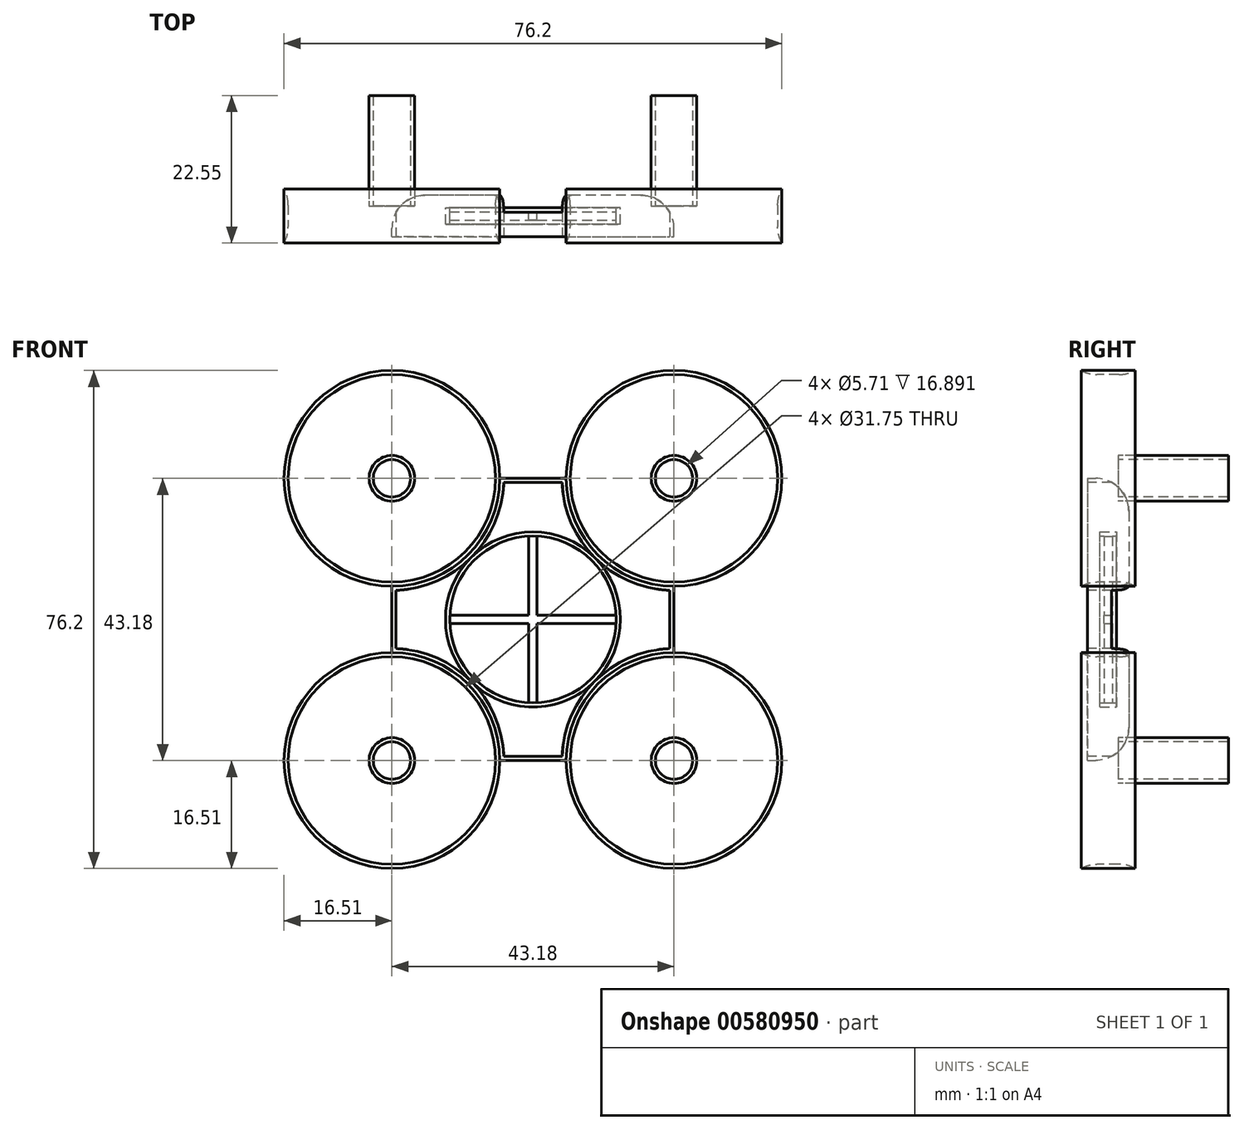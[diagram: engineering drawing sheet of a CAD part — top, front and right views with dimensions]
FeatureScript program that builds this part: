
annotation { "Feature Type Name" : "Feature", "Feature Type Description" : "" }
export const myFeature = defineFeature(function(context is Context, id is Id, definition is map)
    precondition{}
    {
        {
            var Q0;
            Q0=qCreatedBy(makeId("Front.planeOp"),FACE);
            var sketch = newSketch(context, id + "F0", { "sketchPlane" : qUnion([Q0])});
            skPoint(sketch, "E0.middle", {"position": v(0, 0) * mm});
            skCircle(sketch, "E1", {"center": v(-21.6, 21.59) * mm, "radius": 16.51 * mm});
            skCircle(sketch, "E2.1.0", {"center": v(21.59, 21.6) * mm, "radius": 16.51 * mm});
            skCircle(sketch, "E2.2.0", {"center": v(21.6, -21.59) * mm, "radius": 16.51 * mm});
            skCircle(sketch, "E2.3.0", {"center": v(-21.59, -21.6) * mm, "radius": 16.51 * mm});
            skLineSegment(sketch, "E3.bottom", {"start": v(5.08, 21.6) * mm, "end": v(-5.08, 21.6) * mm});
            skLineSegment(sketch, "E3.top", {"start": v(5.08, -21.6) * mm, "end": v(-5.08, -21.6) * mm});
            skLineSegment(sketch, "E3.left", {"start": v(21.59, 5.08) * mm, "end": v(21.59, -5.08) * mm});
            skLineSegment(sketch, "E3.right", {"start": v(-21.59, 5.08) * mm, "end": v(-21.59, -5.08) * mm});
            skPoint(sketch, "E4.orphan", {"position": v(-21.59, 21.6) * mm});
            skPoint(sketch, "E5.orphan", {"position": v(21.59, -21.6) * mm});
            skSolve(sketch);
        }
        {
            var Q0;
            {var subQ0=sQuery(id+"F0.wireOp",EDGE,"E1");var subQ1=makeQuery(id+"F0.imprint","INTERSECT",VERTEX,{"derivedFrom":[subQ0,sQuery(id+"F0.wireOp",EDGE,"E3.bottom")]});Q0=makeQuery(id+"F0.imprint","IMPRINT",FACE,{"disambiguationData":[TD([[makeQuery(id+"F0.imprint","IMPRINT",EDGE,{"disambiguationData":[TD([[subQ1,-1.0]])],"derivedFrom":subQ0}),1.0]])]});}
            var Q1;
            {var subQ0=sQuery(id+"F0.wireOp",EDGE,"E2.3.0");var subQ1=makeQuery(id+"F0.imprint","INTERSECT",VERTEX,{"derivedFrom":[subQ0,sQuery(id+"F0.wireOp",EDGE,"E3.top")]});Q1=makeQuery(id+"F0.imprint","IMPRINT",FACE,{"disambiguationData":[TD([[makeQuery(id+"F0.imprint","IMPRINT",EDGE,{"disambiguationData":[TD([[subQ1,1.0]])],"derivedFrom":subQ0}),1.0]])]});}
            var Q2;
            {var subQ0=sQuery(id+"F0.wireOp",EDGE,"E2.2.0");var subQ1=makeQuery(id+"F0.imprint","INTERSECT",VERTEX,{"derivedFrom":[subQ0,sQuery(id+"F0.wireOp",EDGE,"E3.top")]});Q2=makeQuery(id+"F0.imprint","IMPRINT",FACE,{"disambiguationData":[TD([[makeQuery(id+"F0.imprint","IMPRINT",EDGE,{"disambiguationData":[TD([[subQ1,-1.0]])],"derivedFrom":subQ0}),1.0]])]});}
            var Q3;
            {var subQ0=sQuery(id+"F0.wireOp",EDGE,"E2.1.0");var subQ1=makeQuery(id+"F0.imprint","INTERSECT",VERTEX,{"derivedFrom":[subQ0,sQuery(id+"F0.wireOp",EDGE,"E3.bottom")]});Q3=makeQuery(id+"F0.imprint","IMPRINT",FACE,{"disambiguationData":[TD([[makeQuery(id+"F0.imprint","IMPRINT",EDGE,{"disambiguationData":[TD([[subQ1,1.0]])],"derivedFrom":subQ0}),1.0]])]});}
            extrude(context, id + "F1", {"entities" : qUnion([Q0, Q1, Q2, Q3]), "depth" : 8.25 * mm, "offsetDistance" : 25.4 * mm, "symmetric" : true});
        }
        {
            var Q0;
            {var subQ5=sQuery(id+"F0.wireOp",EDGE,"E3.bottom");Q0=makeQuery(id+"F0.imprint","IMPRINT",FACE,{"disambiguationData":[TD([[makeQuery(id+"F0.imprint","IMPRINT",EDGE,{"derivedFrom":subQ5}),1.0]])]});}
            extrude(context, id + "F2", {"entities" : qUnion([Q0]), "depth" : 6.35 * mm, "offsetDistance" : 25.4 * mm, "symmetric" : true});
        }
        {
            var Q0;
            Q0=makeQuery(id+"F1.opExtrude","CAP_FACE",FACE,{"disambiguationData":[OSD([sQuery(id+"F0.wireOp",EDGE,"E1")])],"isStart":false});
            var sketch = newSketch(context, id + "F3", { "sketchPlane" : qUnion([Q0])});
            skCircle(sketch, "E6", {"center": v(-21.6, 21.59) * mm, "radius": 15.88 * mm});
            skCircle(sketch, "E7.1.0", {"center": v(21.59, 21.6) * mm, "radius": 15.88 * mm});
            skCircle(sketch, "E7.2.0", {"center": v(21.6, -21.59) * mm, "radius": 15.88 * mm});
            skCircle(sketch, "E7.3.0", {"center": v(-21.59, -21.6) * mm, "radius": 15.88 * mm});
            skPoint(sketch, "E7.center", {"position": v(0, 0) * mm});
            skLineSegment(sketch, "E7.anchor1", {"start": v(0, 0) * mm, "end": v(-21.6, 21.59) * mm, "construction": true});
            skLineSegment(sketch, "E7.anchor2", {"start": v(0, 0) * mm, "end": v(-21.59, -21.6) * mm, "construction": true});
            skSolve(sketch);
        }
        {
            var Q0;
            Q0=makeQuery(id+"F3.imprint","IMPRINT",FACE,{"disambiguationData":[TD([[makeQuery(id+"F3.imprint","IMPRINT",EDGE,{"derivedFrom":sQuery(id+"F3.wireOp",EDGE,"E6")}),1.0]])]});
            var Q1;
            Q1=makeQuery(id+"F3.imprint","IMPRINT",FACE,{"disambiguationData":[TD([[makeQuery(id+"F3.imprint","IMPRINT",EDGE,{"derivedFrom":sQuery(id+"F3.wireOp",EDGE,"E7.1.0")}),1.0]])]});
            var Q2;
            Q2=makeQuery(id+"F3.imprint","IMPRINT",FACE,{"disambiguationData":[TD([[makeQuery(id+"F3.imprint","IMPRINT",EDGE,{"derivedFrom":sQuery(id+"F3.wireOp",EDGE,"E7.2.0")}),1.0]])]});
            var Q3;
            Q3=makeQuery(id+"F3.imprint","IMPRINT",FACE,{"disambiguationData":[TD([[makeQuery(id+"F3.imprint","IMPRINT",EDGE,{"derivedFrom":sQuery(id+"F3.wireOp",EDGE,"E7.3.0")}),1.0]])]});
            extrude(context, id + "F4", {"entities" : qUnion([Q0, Q1, Q2, Q3]), "operationType" : NewBodyOperationType.REMOVE, "oppositeDirection" : true, "depth" : 25.4 * mm, "offsetDistance" : 25.4 * mm});
        }
        {
            var Q0;
            Q0=makeQuery(id+"F2.opExtrude","CAP_FACE",FACE,{"disambiguationData":[OSD([sQuery(id+"F0.wireOp",EDGE,"E1"),sQuery(id+"F0.wireOp",EDGE,"E2.1.0"),sQuery(id+"F0.wireOp",EDGE,"E2.2.0"),sQuery(id+"F0.wireOp",EDGE,"E2.3.0"),sQuery(id+"F0.wireOp",EDGE,"E3.bottom"),sQuery(id+"F0.wireOp",EDGE,"E3.top"),sQuery(id+"F0.wireOp",EDGE,"E3.left"),sQuery(id+"F0.wireOp",EDGE,"E3.right")])],"isStart":false});
            var sketch = newSketch(context, id + "F5", { "sketchPlane" : qUnion([Q0])});
            skLineSegment(sketch, "E8.0", {"start": v(4.46, 20.96) * mm, "end": v(-4.46, 20.96) * mm});
            skArc(sketch, "E8.1", {"start": v(20.95, 4.46) * mm, "mid": v(9.47, 9.47) * mm, "end": v(4.46, 20.96) * mm});
            skArc(sketch, "E8.2", {"start": v(-4.46, 20.96) * mm, "mid": v(-9.47, 9.47) * mm, "end": v(-20.95, 4.46) * mm});
            skLineSegment(sketch, "E8.3", {"start": v(20.95, -4.46) * mm, "end": v(20.95, 4.46) * mm});
            skLineSegment(sketch, "E8.4", {"start": v(-20.95, 4.46) * mm, "end": v(-20.95, -4.46) * mm});
            skArc(sketch, "E8.5", {"start": v(-20.95, -4.46) * mm, "mid": v(-9.47, -9.47) * mm, "end": v(-4.46, -20.96) * mm});
            skLineSegment(sketch, "E8.6", {"start": v(-4.46, -20.96) * mm, "end": v(4.46, -20.96) * mm});
            skArc(sketch, "E8.7", {"start": v(4.46, -20.96) * mm, "mid": v(9.47, -9.47) * mm, "end": v(20.95, -4.46) * mm});
            skSolve(sketch);
        }
        {
            var Q0;
            Q0=makeQuery(id+"F5.imprint","IMPRINT",FACE,{"disambiguationData":[TD([[makeQuery(id+"F5.imprint","IMPRINT",EDGE,{"derivedFrom":sQuery(id+"F5.wireOp",EDGE,"E8.0")}),1.0]])]});
            extrude(context, id + "F6", {"entities" : qUnion([Q0]), "operationType" : NewBodyOperationType.REMOVE, "oppositeDirection" : true, "depth" : 25.4 * mm, "offsetDistance" : 25.4 * mm});
        }
        {
            var Q0;
            Q0=makeQuery(id+"F4.boolean.opBoolean","COPY",FACE,{"derivedFrom":makeQuery(id+"F4.opExtrude","SWEPT_FACE",FACE,{"disambiguationData":[OSD([sQuery(id+"F3.wireOp",EDGE,"E7.1.0")])]})});
            var Q1;
            Q1=makeQuery(id+"F4.boolean.opBoolean","COPY",FACE,{"derivedFrom":makeQuery(id+"F4.opExtrude","SWEPT_FACE",FACE,{"disambiguationData":[OSD([sQuery(id+"F3.wireOp",EDGE,"E7.2.0")])]})});
            var Q2;
            Q2=makeQuery(id+"F4.boolean.opBoolean","COPY",FACE,{"derivedFrom":makeQuery(id+"F4.opExtrude","SWEPT_FACE",FACE,{"disambiguationData":[OSD([sQuery(id+"F3.wireOp",EDGE,"E6")])]})});
            var Q3;
            Q3=makeQuery(id+"F4.boolean.opBoolean","COPY",FACE,{"derivedFrom":makeQuery(id+"F4.opExtrude","SWEPT_FACE",FACE,{"disambiguationData":[OSD([sQuery(id+"F3.wireOp",EDGE,"E7.3.0")])]})});
            fillet(context, id + "F7", {"entities" : qUnion([Q0, Q1, Q2, Q3]), "radius" : 5.08 * mm, "tangentPropagation" : true, "allowEdgeOverflow" : false});
        }
        {
            var Q0;
            Q0=makeQuery(id+"F2.opExtrude","CAP_EDGE",EDGE,{"disambiguationData":[OSD([sQuery(id+"F0.wireOp",EDGE,"E3.bottom")])],"isStart":true});
            var Q1;
            Q1=makeQuery(id+"F2.opExtrude","CAP_EDGE",EDGE,{"disambiguationData":[OSD([sQuery(id+"F0.wireOp",EDGE,"E3.left")])],"isStart":true});
            var Q2;
            Q2=makeQuery(id+"F2.opExtrude","CAP_EDGE",EDGE,{"disambiguationData":[OSD([sQuery(id+"F0.wireOp",EDGE,"E3.right")])],"isStart":true});
            var Q3;
            Q3=makeQuery(id+"F2.opExtrude","CAP_EDGE",EDGE,{"disambiguationData":[OSD([sQuery(id+"F0.wireOp",EDGE,"E3.top")])],"isStart":true});
            fillet(context, id + "F8", {"entities" : qUnion([Q0, Q1, Q2, Q3]), "radius" : 5.08 * mm, "tangentPropagation" : true, "allowEdgeOverflow" : false});
        }
        {
            var Q0;
            Q0=qCreatedBy(makeId("Front.planeOp"),FACE);
            var sketch = newSketch(context, id + "F9", { "sketchPlane" : qUnion([Q0])});
            skCircle(sketch, "E9", {"center": v(0, 0) * mm, "radius": 13.39 * mm});
            skCircle(sketch, "E10", {"center": v(0, 0) * mm, "radius": 12.75 * mm});
            skLineSegment(sketch, "E11.0", {"start": v(-12.73, -0.64) * mm, "end": v(-0.64, -0.64) * mm});
            skLineSegment(sketch, "E12.0", {"start": v(-12.73, 0.64) * mm, "end": v(-0.64, 0.64) * mm});
            skLineSegment(sketch, "E13.0", {"start": v(-0.64, 12.73) * mm, "end": v(-0.64, 0.64) * mm});
            skLineSegment(sketch, "E14.0", {"start": v(0.63, 12.73) * mm, "end": v(0.64, 0.64) * mm});
            skLineSegment(sketch, "E15.trimOffspring", {"start": v(0.64, 0.64) * mm, "end": v(12.73, 0.64) * mm});
            skLineSegment(sketch, "E16.trimOffspring", {"start": v(0.64, -0.64) * mm, "end": v(12.73, -0.64) * mm});
            skLineSegment(sketch, "E17.trimOffspring", {"start": v(-0.64, -0.64) * mm, "end": v(-0.63, -12.73) * mm});
            skLineSegment(sketch, "E18.trimOffspring", {"start": v(0.64, -0.64) * mm, "end": v(0.64, -12.73) * mm});
            skLineSegment(sketch, "E19", {"start": v(-20.95, 0) * mm, "end": v(20.95, 0) * mm, "construction": true});
            skLineSegment(sketch, "E20", {"start": v(0, 20.96) * mm, "end": v(0, -20.96) * mm, "construction": true});
            skSolve(sketch);
        }
        {
            var Q0;
            Q0=makeQuery(id+"F9.imprint","IMPRINT",FACE,{"disambiguationData":[TD([[makeQuery(id+"F9.imprint","IMPRINT",EDGE,{"derivedFrom":sQuery(id+"F9.wireOp",EDGE,"E10")}),-1.0]])]});
            extrude(context, id + "F10", {"entities" : qUnion([Q0]), "depth" : 2.54 * mm, "offsetDistance" : 25.4 * mm, "symmetric" : true});
        }
        {
            var Q0;
            {var subQ4=sQuery(id+"F9.wireOp",EDGE,"E11.0");Q0=makeQuery(id+"F9.imprint","IMPRINT",FACE,{"disambiguationData":[TD([[makeQuery(id+"F9.imprint","IMPRINT",EDGE,{"derivedFrom":subQ4}),1.0]])]});}
            extrude(context, id + "F11", {"entities" : qUnion([Q0]), "operationType" : NewBodyOperationType.ADD, "depth" : 1.27 * mm, "offsetDistance" : 25.4 * mm, "symmetric" : true});
        }
        {
            var Q0;
            Q0=makeQuery(id+"F8.opFillet","SPLIT",FACE,{"disambiguationData":[OD(0.0)],"derivedFrom":makeQuery(id+"F2.opExtrude","CAP_FACE",FACE,{"disambiguationData":[OSD([sQuery(id+"F0.wireOp",EDGE,"E1"),sQuery(id+"F0.wireOp",EDGE,"E2.1.0"),sQuery(id+"F0.wireOp",EDGE,"E2.2.0"),sQuery(id+"F0.wireOp",EDGE,"E2.3.0"),sQuery(id+"F0.wireOp",EDGE,"E3.bottom"),sQuery(id+"F0.wireOp",EDGE,"E3.top"),sQuery(id+"F0.wireOp",EDGE,"E3.left"),sQuery(id+"F0.wireOp",EDGE,"E3.right")])],"isStart":true})});
            var sketch = newSketch(context, id + "F12", { "sketchPlane" : qUnion([Q0])});
            skCircle(sketch, "E21", {"center": v(21.6, 21.59) * mm, "radius": 2.86 * mm});
            skCircle(sketch, "E22.1.0", {"center": v(-21.59, 21.6) * mm, "radius": 2.86 * mm});
            skCircle(sketch, "E22.2.0", {"center": v(-21.6, -21.59) * mm, "radius": 2.86 * mm});
            skCircle(sketch, "E22.3.0", {"center": v(21.59, -21.6) * mm, "radius": 2.86 * mm});
            skPoint(sketch, "E22.center", {"position": v(0, 0) * mm});
            skCircle(sketch, "E23", {"center": v(21.6, 21.59) * mm, "radius": 3.5 * mm});
            skCircle(sketch, "E24.1.0", {"center": v(21.59, -21.6) * mm, "radius": 3.5 * mm});
            skCircle(sketch, "E24.2.0", {"center": v(-21.59, -21.59) * mm, "radius": 3.5 * mm});
            skCircle(sketch, "E24.3.0", {"center": v(-21.59, 21.59) * mm, "radius": 3.5 * mm});
            skLineSegment(sketch, "E24.anchor1", {"start": v(0, 0) * mm, "end": v(21.6, 21.59) * mm, "construction": true});
            skLineSegment(sketch, "E24.anchor2", {"start": v(0, 0) * mm, "end": v(-21.59, 21.59) * mm, "construction": true});
            skSolve(sketch);
        }
        {
            var Q0;
            Q0=makeQuery(id+"F12.imprint","IMPRINT",FACE,{"disambiguationData":[TD([[makeQuery(id+"F12.imprint","IMPRINT",EDGE,{"derivedFrom":sQuery(id+"F12.wireOp",EDGE,"E21")}),-1.0]])]});
            var Q1;
            Q1=makeQuery(id+"F12.imprint","IMPRINT",FACE,{"disambiguationData":[TD([[makeQuery(id+"F12.imprint","IMPRINT",EDGE,{"derivedFrom":sQuery(id+"F12.wireOp",EDGE,"E22.1.0")}),-1.0]])]});
            var Q2;
            Q2=makeQuery(id+"F12.imprint","IMPRINT",FACE,{"disambiguationData":[TD([[makeQuery(id+"F12.imprint","IMPRINT",EDGE,{"derivedFrom":sQuery(id+"F12.wireOp",EDGE,"E22.2.0")}),-1.0]])]});
            var Q3;
            Q3=makeQuery(id+"F12.imprint","IMPRINT",FACE,{"disambiguationData":[TD([[makeQuery(id+"F12.imprint","IMPRINT",EDGE,{"derivedFrom":sQuery(id+"F12.wireOp",EDGE,"E22.3.0")}),-1.0]])]});
            extrude(context, id + "F13", {"entities" : qUnion([Q0, Q1, Q2, Q3]), "depth" : 15.24 * mm, "offsetDistance" : 12.7 * mm, "hasSecondDirection" : true, "secondDirectionOppositeDirection" : true, "secondDirectionDepth" : 1.65 * mm});
        }
    });
